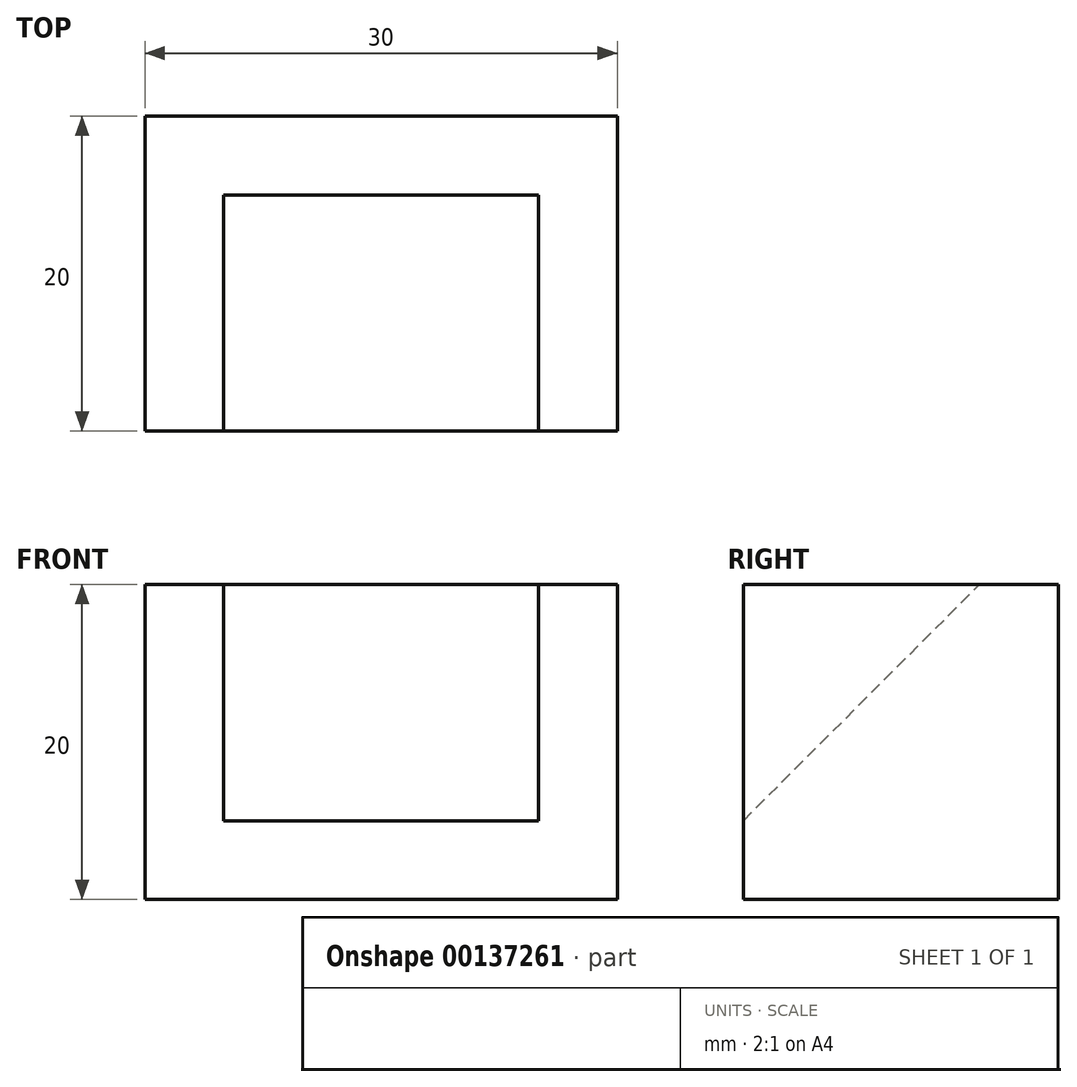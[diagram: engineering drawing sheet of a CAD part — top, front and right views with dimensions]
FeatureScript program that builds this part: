
annotation { "Feature Type Name" : "Feature", "Feature Type Description" : "" }
export const myFeature = defineFeature(function(context is Context, id is Id, definition is map)
    precondition{}
    {
        {
            var Q0;
            Q0=qCreatedBy(makeId("Front.planeOp"),FACE);
            var sketch = newSketch(context, id + "F0", { "sketchPlane" : qUnion([Q0])});
            skLineSegment(sketch, "E0.bottom", {"start": v(0, 0) * mm, "end": v(30, 0) * mm});
            skLineSegment(sketch, "E0.top", {"start": v(0, 20) * mm, "end": v(30, 20) * mm});
            skLineSegment(sketch, "E0.left", {"start": v(0, 0) * mm, "end": v(0, 20) * mm});
            skLineSegment(sketch, "E0.right", {"start": v(30, 0) * mm, "end": v(30, 20) * mm});
            skSolve(sketch);
        }
        {
            var Q0;
            Q0 = qSketchRegion(id + "F0", true);
            extrude(context, id + "F1", {"entities" : qUnion([Q0]), "endBound" : BoundingType.SYMMETRIC, "depth" : 20 * mm});
        }
        {
            var Q0;
            Q0=makeQuery(id+"F1.opExtrude","SWEPT_FACE",FACE,{"disambiguationData":[OSD([sQuery(id+"F0.wireOp",EDGE,"E0.right")])]});
            var sketch = newSketch(context, id + "F2", { "sketchPlane" : qUnion([Q0])});
            skLineSegment(sketch, "E1", {"start": v(-10, 20) * mm, "end": v(-10, 5) * mm});
            skLineSegment(sketch, "E2", {"start": v(-10, 5) * mm, "end": v(5, 20) * mm});
            skLineSegment(sketch, "E3", {"start": v(5, 20) * mm, "end": v(-10, 20) * mm});
            skSolve(sketch);
        }
        {
            var Q0;
            Q0=makeQuery(id+"F2.imprint","IMPRINT",FACE,{"disambiguationData":[TD([[makeQuery(id+"F2.imprint","IMPRINT",EDGE,{"derivedFrom":sQuery(id+"F2.wireOp",EDGE,"E1")}),-1.0]])]});
            extrude(context, id + "F3", {"entities" : qUnion([Q0]), "operationType" : NewBodyOperationType.REMOVE, "oppositeDirection" : true, "depth" : 25 * mm});
        }
        {
            var Q0;
            Q0=makeQuery(id+"F1.opExtrude","SWEPT_FACE",FACE,{"disambiguationData":[OSD([sQuery(id+"F0.wireOp",EDGE,"E0.right")])]});
            var sketch = newSketch(context, id + "F4", { "sketchPlane" : qUnion([Q0])});
            skLineSegment(sketch, "E4", {"start": v(-10, 5) * mm, "end": v(-10, 20) * mm});
            skLineSegment(sketch, "E5", {"start": v(5, 20) * mm, "end": v(-10, 20) * mm});
            skSolve(sketch);
        }
        {
            var Q0;
            Q0=makeQuery(id+"F4.imprint","IMPRINT",FACE,{"disambiguationData":[TD([[makeQuery(id+"F4.imprint","IMPRINT",EDGE,{"derivedFrom":sQuery(id+"F4.wireOp",EDGE,"E4")}),-1.0]])]});
            extrude(context, id + "F5", {"entities" : qUnion([Q0]), "operationType" : NewBodyOperationType.ADD, "oppositeDirection" : true, "depth" : 5 * mm});
        }
    });
